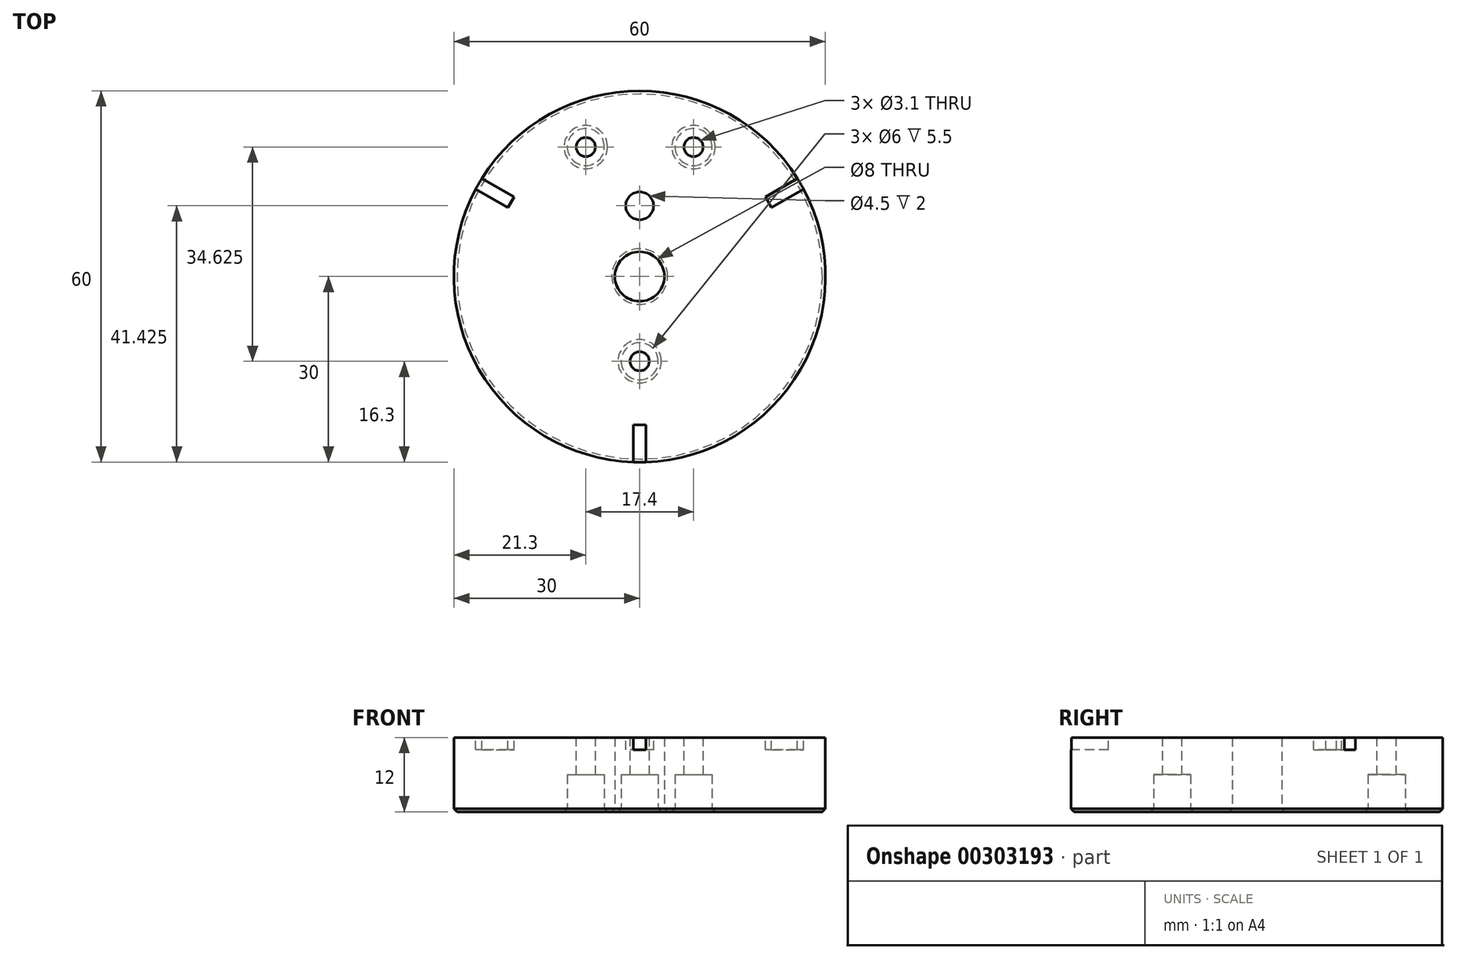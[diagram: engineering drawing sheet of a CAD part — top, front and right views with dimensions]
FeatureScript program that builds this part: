
annotation { "Feature Type Name" : "Feature", "Feature Type Description" : "" }
export const myFeature = defineFeature(function(context is Context, id is Id, definition is map)
    precondition{}
    {
        {
            var Q0;
            Q0=qCreatedBy(makeId("Top.planeOp"),FACE);
            var sketch = newSketch(context, id + "F0", { "sketchPlane" : qUnion([Q0])});
            skCircle(sketch, "E0", {"center": v(0, 0) * mm, "radius": 4 * mm});
            skCircle(sketch, "E1", {"center": v(0, 0) * mm, "radius": 30 * mm});
            skSolve(sketch);
        }
        {
            var Q0;
            Q0 = qSketchRegion(id + "F0", true);
            extrude(context, id + "F1", {"entities" : qUnion([Q0]), "depth" : 12 * mm});
        }
        {
            var Q0;
            Q0=makeQuery(id+"F1.opExtrude","CAP_FACE",FACE,{"disambiguationData":[OSD([sQuery(id+"F0.wireOp",EDGE,"E0"),sQuery(id+"F0.wireOp",EDGE,"E1")])],"isStart":false});
            var sketch = newSketch(context, id + "F2", { "sketchPlane" : qUnion([Q0])});
            skCircle(sketch, "E2", {"center": v(0, 11.43) * mm, "radius": 2.25 * mm});
            skSolve(sketch);
        }
        {
            var Q0;
            Q0 = qSketchRegion(id + "F2", true);
            extrude(context, id + "F3", {"entities" : qUnion([Q0]), "operationType" : NewBodyOperationType.REMOVE, "oppositeDirection" : true, "depth" : 2 * mm});
        }
        {
            var Q0;
            Q0=makeQuery(id+"F1.opExtrude","CAP_FACE",FACE,{"disambiguationData":[OSD([sQuery(id+"F0.wireOp",EDGE,"E0"),sQuery(id+"F0.wireOp",EDGE,"E1")])],"isStart":false});
            var sketch = newSketch(context, id + "F4", { "sketchPlane" : qUnion([Q0])});
            skLineSegment(sketch, "E3", {"start": v(-21.5, 20.93) * mm, "end": v(21.5, 20.93) * mm, "construction": true});
            skCircle(sketch, "E4.0", {"center": v(0, 11.43) * mm, "radius": 2.25 * mm, "construction": true});
            skCircle(sketch, "E5", {"center": v(8.7, 20.93) * mm, "radius": 1.55 * mm});
            skCircle(sketch, "E6.MirrorC", {"center": v(-8.7, 20.93) * mm, "radius": 1.55 * mm});
            skCircle(sketch, "E7", {"center": v(0, -13.7) * mm, "radius": 1.55 * mm});
            skSolve(sketch);
        }
        {
            var Q0;
            Q0 = qSketchRegion(id + "F4", true);
            extrude(context, id + "F5", {"entities" : qUnion([Q0]), "operationType" : NewBodyOperationType.REMOVE, "oppositeDirection" : true, "depth" : 25 * mm});
        }
        {
            var Q0;
            Q0=makeQuery(id+"F1.opExtrude","CAP_FACE",FACE,{"disambiguationData":[OSD([sQuery(id+"F0.wireOp",EDGE,"E0"),sQuery(id+"F0.wireOp",EDGE,"E1")])],"isStart":true});
            var sketch = newSketch(context, id + "F6", { "sketchPlane" : qUnion([Q0])});
            skCircle(sketch, "E8.0.0", {"center": v(0, 0) * mm, "radius": 30 * mm, "construction": true});
            skCircle(sketch, "E9.0", {"center": v(-8.7, -20.93) * mm, "radius": 1.55 * mm, "construction": true});
            skCircle(sketch, "E10.0", {"center": v(8.7, -20.93) * mm, "radius": 1.55 * mm, "construction": true});
            skCircle(sketch, "E11.0", {"center": v(0, 13.7) * mm, "radius": 1.55 * mm, "construction": true});
            skCircle(sketch, "E12", {"center": v(0, 13.7) * mm, "radius": 3 * mm});
            skCircle(sketch, "E13", {"center": v(-8.7, -20.93) * mm, "radius": 3 * mm});
            skCircle(sketch, "E14", {"center": v(8.7, -20.93) * mm, "radius": 3 * mm});
            skSolve(sketch);
        }
        {
            var Q0;
            Q0 = qSketchRegion(id + "F6", true);
            extrude(context, id + "F7", {"entities" : qUnion([Q0]), "operationType" : NewBodyOperationType.REMOVE, "oppositeDirection" : true, "depth" : 6 * mm});
        }
        {
            var Q0;
            Q0=makeQuery(id+"F1.opExtrude","CAP_FACE",FACE,{"disambiguationData":[OSD([sQuery(id+"F0.wireOp",EDGE,"E0"),sQuery(id+"F0.wireOp",EDGE,"E1")])],"isStart":false});
            var sketch = newSketch(context, id + "F8", { "sketchPlane" : qUnion([Q0])});
            skLineSegment(sketch, "E15", {"start": v(0, 0) * mm, "end": v(25.98, 15) * mm, "construction": true});
            skLineSegment(sketch, "E16", {"start": v(0, 0) * mm, "end": v(0, -30) * mm, "construction": true});
            skLineSegment(sketch, "E17", {"start": v(0, 0) * mm, "end": v(-25.98, 15) * mm, "construction": true});
            skArc(sketch, "E18.0", {"start": v(26.47, 14.13) * mm, "mid": v(25.98, 15) * mm, "end": v(25.47, 15.86) * mm});
            skLineSegment(sketch, "E19", {"start": v(1, -24) * mm, "end": v(1, -29.98) * mm});
            skLineSegment(sketch, "E20", {"start": v(-1, -29.98) * mm, "end": v(-1, -24) * mm});
            skLineSegment(sketch, "E21", {"start": v(-1, -24) * mm, "end": v(1, -24) * mm});
            skLineSegment(sketch, "E22", {"start": v(21.28, 11.13) * mm, "end": v(26.47, 14.13) * mm});
            skLineSegment(sketch, "E23", {"start": v(25.47, 15.86) * mm, "end": v(20.28, 12.87) * mm});
            skLineSegment(sketch, "E24", {"start": v(21.28, 11.13) * mm, "end": v(20.28, 12.87) * mm});
            skLineSegment(sketch, "E25", {"start": v(-25.47, 15.86) * mm, "end": v(-20.28, 12.87) * mm});
            skLineSegment(sketch, "E26", {"start": v(-20.28, 12.87) * mm, "end": v(-21.28, 11.13) * mm});
            skLineSegment(sketch, "E27", {"start": v(-21.28, 11.13) * mm, "end": v(-26.47, 14.13) * mm});
            skArc(sketch, "E28.trimOffspring", {"start": v(-25.47, 15.86) * mm, "mid": v(-25.98, 15) * mm, "end": v(-26.47, 14.13) * mm});
            skArc(sketch, "E29.trimOffspring", {"start": v(-1, -29.98) * mm, "mid": v(0, -30) * mm, "end": v(1, -29.98) * mm});
            skSolve(sketch);
        }
        {
            var Q0;
            Q0 = qSketchRegion(id + "F8", true);
            extrude(context, id + "F9", {"entities" : qUnion([Q0]), "operationType" : NewBodyOperationType.REMOVE, "oppositeDirection" : true, "depth" : 2 * mm});
        }
        {
            var Q0;
            Q0=makeQuery(id+"F1.opExtrude","CAP_FACE",FACE,{"disambiguationData":[OSD([sQuery(id+"F0.wireOp",EDGE,"E0"),sQuery(id+"F0.wireOp",EDGE,"E1")])],"isStart":true});
            chamfer(context, id + "F10", {"entities" : qUnion([Q0]), "width" : 0.5 * mm, "tangentPropagation" : true});
        }
    });
